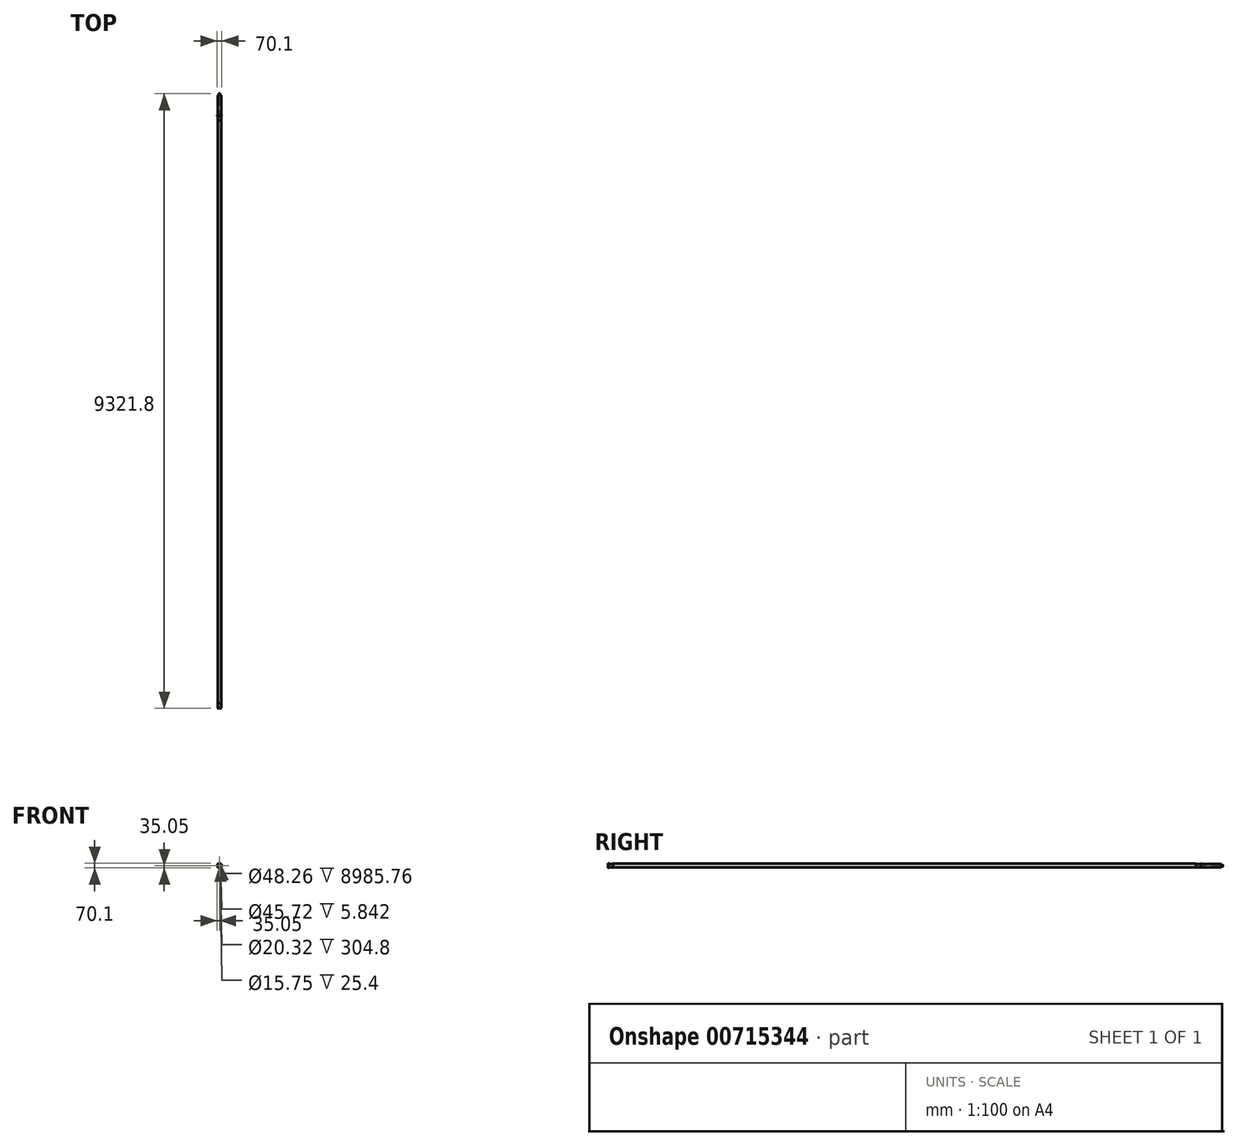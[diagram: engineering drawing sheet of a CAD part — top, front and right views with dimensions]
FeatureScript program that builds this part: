
annotation { "Feature Type Name" : "Feature", "Feature Type Description" : "" }
export const myFeature = defineFeature(function(context is Context, id is Id, definition is map)
    precondition{}
    {
        {
            var Q0;
            Q0=qCreatedBy(makeId("Front.planeOp"),FACE);
            var sketch = newSketch(context, id + "F0", { "sketchPlane" : qUnion([Q0])});
            skCircle(sketch, "E0", {"center": v(0, 0) * mm, "radius": 22.23 * mm, "construction": true});
            skSolve(sketch);
        }
        {
            var Q0;
            Q0=qCreatedBy(makeId("Front.planeOp"),FACE);
            var sketch = newSketch(context, id + "F1", { "sketchPlane" : qUnion([Q0])});
            skCircle(sketch, "E1", {"center": v(0, 0) * mm, "radius": 24.13 * mm});
            skCircle(sketch, "E2", {"center": v(0, 0) * mm, "radius": 35.05 * mm});
            skSolve(sketch);
        }
        {
            var Q0;
            Q0=qSketchRegion(id+"F1",true);
            extrude(context, id + "F2", {"entities" : qUnion([Q0]), "oppositeDirection" : true, "depth" : 5.84 * mm, "offsetDistance" : 25.4 * mm});
        }
        {
            var Q0;
            Q0=makeQuery(id+"F2.opExtrude","CAP_EDGE",EDGE,{"disambiguationData":[OSD([sQuery(id+"F1.wireOp",EDGE,"E2")])],"isStart":false});
            chamfer(context, id + "F3", {"entities" : qUnion([Q0]), "chamferType" : ChamferType.OFFSET_ANGLE, "width" : 2.54 * mm, "oppositeDirection" : false, "angle" : 70 * degree, "tangentPropagation" : true});
        }
        {
            var Q0;
            Q0=makeQuery(id+"F2.opExtrude","CAP_FACE",FACE,{"disambiguationData":[OSD([sQuery(id+"F1.wireOp",EDGE,"E1"),sQuery(id+"F1.wireOp",EDGE,"E2")])],"isStart":false});
            var sketch = newSketch(context, id + "F4", { "sketchPlane" : qUnion([Q0])});
            skCircle(sketch, "E3", {"center": v(0, 0) * mm, "radius": 28.07 * mm});
            skCircle(sketch, "E4", {"center": v(0, 0) * mm, "radius": 24.13 * mm});
            skSolve(sketch);
        }
        {
            var Q0;
            Q0=qSketchRegion(id+"F4",true);
            extrude(context, id + "F5", {"entities" : qUnion([Q0]), "operationType" : NewBodyOperationType.ADD, "depth" : 2.54 * mm, "offsetDistance" : 25.4 * mm});
        }
        {
            var Q0;
            Q0=makeQuery(id+"F5.opExtrude","CAP_FACE",FACE,{"disambiguationData":[OSD([sQuery(id+"F4.wireOp",EDGE,"E3"),sQuery(id+"F4.wireOp",EDGE,"E4")])],"isStart":false});
            var sketch = newSketch(context, id + "F6", { "sketchPlane" : qUnion([Q0])});
            skCircle(sketch, "E5", {"center": v(0, 0) * mm, "radius": 26.55 * mm});
            skCircle(sketch, "E6", {"center": v(0, 0) * mm, "radius": 24.13 * mm});
            skSolve(sketch);
        }
        {
            var Q0;
            Q0=qSketchRegion(id+"F6",true);
            extrude(context, id + "F7", {"entities" : qUnion([Q0]), "operationType" : NewBodyOperationType.ADD, "depth" : 2.54 * mm, "offsetDistance" : 25.4 * mm});
        }
        {
            var Q0;
            Q0=makeQuery(id+"F7.opExtrude","CAP_FACE",FACE,{"disambiguationData":[OSD([sQuery(id+"F6.wireOp",EDGE,"E5"),sQuery(id+"F6.wireOp",EDGE,"E6")])],"isStart":false});
            var sketch = newSketch(context, id + "F8", { "sketchPlane" : qUnion([Q0])});
            skCircle(sketch, "E7", {"center": v(0, 0) * mm, "radius": 24.13 * mm});
            skCircle(sketch, "E8", {"center": v(0, 0) * mm, "radius": 25.4 * mm});
            skSolve(sketch);
        }
        {
            var Q0;
            Q0=qSketchRegion(id+"F8",true);
            extrude(context, id + "F9", {"entities" : qUnion([Q0]), "operationType" : NewBodyOperationType.ADD, "depth" : 65.28 * mm, "offsetDistance" : 25.4 * mm});
        }
        {
            var Q0;
            Q0=makeQuery(id+"F9.opExtrude","CAP_FACE",FACE,{"disambiguationData":[OSD([sQuery(id+"F8.wireOp",EDGE,"E7"),sQuery(id+"F8.wireOp",EDGE,"E8")])],"isStart":false});
            var sketch = newSketch(context, id + "F10", { "sketchPlane" : qUnion([Q0])});
            skCircle(sketch, "E9", {"center": v(0, 0) * mm, "radius": 27.94 * mm});
            skCircle(sketch, "E10", {"center": v(0, 0) * mm, "radius": 24.13 * mm});
            skSolve(sketch);
        }
        {
            var Q0;
            Q0=qCreatedBy(makeId("Right.planeOp"),FACE);
            var sketch = newSketch(context, id + "F11", { "sketchPlane" : qUnion([Q0])});
            skLineSegment(sketch, "E11", {"start": v(76.2, 0) * mm, "end": v(8915.4, 0) * mm});
            skSolve(sketch);
        }
        {
            var Q0;
            Q0=qSketchRegion(id+"F10",true);
            var Q1;
            Q1=qConstructionFilter(qBodyType(qCreatedBy(id+"F11",EDGE),BodyType.WIRE),ConstructionObject.NO);
            sweep(context, id + "F12", {"operationType" : NewBodyOperationType.ADD, "profiles" : qUnion([Q0]), "path" : qUnion([Q1])});
        }
        {
            var Q0;
            Q0=makeQuery(id+"F12.opSweep","CAP_FACE",FACE,{"disambiguationData":[OSD([sQuery(id+"F10.wireOp",EDGE,"E9"),sQuery(id+"F10.wireOp",EDGE,"E10"),sQuery(id+"F11.wireOp",VERTEX,"7ykRA0Qg-2DrY-rTCa-7tXY-ZQoEE0Xzwcjr.end")])],"isStart":false});
            var sketch = newSketch(context, id + "F13", { "sketchPlane" : qUnion([Q0])});
            skCircle(sketch, "E12", {"center": v(0, 0) * mm, "radius": 24.13 * mm});
            skCircle(sketch, "E13", {"center": v(0, 0) * mm, "radius": 25.4 * mm});
            skSolve(sketch);
        }
        {
            var Q0;
            Q0=makeQuery(id+"F12.opSweep","CAP_EDGE",EDGE,{"disambiguationData":[OSD([sQuery(id+"F10.wireOp",EDGE,"E9"),sQuery(id+"F11.wireOp",VERTEX,"7ykRA0Qg-2DrY-rTCa-7tXY-ZQoEE0Xzwcjr.end")])],"isStart":false});
            fillet(context, id + "F14", {"entities" : qUnion([Q0]), "radius" : 1.27 * mm, "tangentPropagation" : true, "allowEdgeOverflow" : false});
        }
        {
            var Q0;
            Q0=qSketchRegion(id+"F13",true);
            extrude(context, id + "F15", {"entities" : qUnion([Q0]), "operationType" : NewBodyOperationType.ADD, "depth" : 76.2 * mm, "offsetDistance" : 25.4 * mm});
        }
        {
            var Q0;
            Q0=makeQuery(id+"F15.opExtrude","CAP_FACE",FACE,{"disambiguationData":[OSD([sQuery(id+"F13.wireOp",EDGE,"E12"),sQuery(id+"F13.wireOp",EDGE,"E13")])],"isStart":false});
            var sketch = newSketch(context, id + "F16", { "sketchPlane" : qUnion([Q0])});
            skCircle(sketch, "E14", {"center": v(0, 0) * mm, "radius": 35.05 * mm});
            skCircle(sketch, "E15", {"center": v(0, 0) * mm, "radius": 22.86 * mm});
            skSolve(sketch);
        }
        {
            var Q0;
            Q0=qSketchRegion(id+"F16",true);
            extrude(context, id + "F17", {"entities" : qUnion([Q0]), "operationType" : NewBodyOperationType.ADD, "oppositeDirection" : true, "depth" : 5.84 * mm, "offsetDistance" : 25.4 * mm});
        }
        {
            var Q0;
            Q0=makeQuery(id+"F17.opExtrude","CAP_EDGE",EDGE,{"disambiguationData":[OSD([sQuery(id+"F16.wireOp",EDGE,"E14")])],"isStart":false});
            chamfer(context, id + "F18", {"entities" : qUnion([Q0]), "chamferType" : ChamferType.OFFSET_ANGLE, "width" : 2.54 * mm, "oppositeDirection" : false, "angle" : 70 * degree, "tangentPropagation" : true});
        }
        {
            var Q0;
            Q0=makeQuery(id+"F17.opExtrude","CAP_FACE",FACE,{"disambiguationData":[OSD([sQuery(id+"F16.wireOp",EDGE,"E14"),sQuery(id+"F16.wireOp",EDGE,"E15")])],"isStart":false});
            var sketch = newSketch(context, id + "F19", { "sketchPlane" : qUnion([Q0])});
            skCircle(sketch, "E16", {"center": v(0, 0) * mm, "radius": 24.13 * mm});
            skCircle(sketch, "E17", {"center": v(0, 0) * mm, "radius": 28.07 * mm});
            skSolve(sketch);
        }
        {
            var Q0;
            Q0=qSketchRegion(id+"F19",true);
            extrude(context, id + "F20", {"entities" : qUnion([Q0]), "operationType" : NewBodyOperationType.ADD, "depth" : 2.54 * mm, "offsetDistance" : 25.4 * mm});
        }
        {
            var Q0;
            Q0=makeQuery(id+"F20.opExtrude","CAP_FACE",FACE,{"disambiguationData":[OSD([sQuery(id+"F19.wireOp",EDGE,"E16"),sQuery(id+"F19.wireOp",EDGE,"E17")])],"isStart":false});
            var sketch = newSketch(context, id + "F21", { "sketchPlane" : qUnion([Q0])});
            skCircle(sketch, "E18", {"center": v(0, 0) * mm, "radius": 24.13 * mm});
            skCircle(sketch, "E19", {"center": v(0, 0) * mm, "radius": 26.8 * mm});
            skSolve(sketch);
        }
        {
            var Q0;
            Q0=qSketchRegion(id+"F21",true);
            extrude(context, id + "F22", {"entities" : qUnion([Q0]), "operationType" : NewBodyOperationType.ADD, "depth" : 2.54 * mm, "offsetDistance" : 25.4 * mm});
        }
        {
            var Q0;
            Q0=makeQuery(id+"F17.boolean.opBoolean","MERGE",FACE,{"derivedFrom":[makeQuery(id+"F15.opExtrude","CAP_FACE",FACE,{"disambiguationData":[OSD([sQuery(id+"F13.wireOp",EDGE,"E12"),sQuery(id+"F13.wireOp",EDGE,"E13")])],"isStart":false}),makeQuery(id+"F17.opExtrude","CAP_FACE",FACE,{"disambiguationData":[OSD([sQuery(id+"F16.wireOp",EDGE,"E14"),sQuery(id+"F16.wireOp",EDGE,"E15")])],"isStart":true})]});
            var sketch = newSketch(context, id + "F23", { "sketchPlane" : qUnion([Q0])});
            skCircle(sketch, "E20", {"center": v(0, 0) * mm, "radius": 10.16 * mm});
            skCircle(sketch, "E21", {"center": v(0, 0) * mm, "radius": 24.13 * mm});
            skSolve(sketch);
        }
        {
            var Q0;
            Q0=qSketchRegion(id+"F23",true);
            extrude(context, id + "F24", {"entities" : qUnion([Q0]), "operationType" : NewBodyOperationType.ADD, "depth" : 304.8 * mm, "offsetDistance" : 25.4 * mm});
        }
        {
            var Q0;
            Q0=makeQuery(id+"F24.opExtrude","CAP_FACE",FACE,{"disambiguationData":[OSD([sQuery(id+"F23.wireOp",EDGE,"E20"),sQuery(id+"F23.wireOp",EDGE,"E21")])],"isStart":false});
            var sketch = newSketch(context, id + "F25", { "sketchPlane" : qUnion([Q0])});
            skCircle(sketch, "E22", {"center": v(0, 0) * mm, "radius": 10.67 * mm});
            skCircle(sketch, "E23", {"center": v(0, 0) * mm, "radius": 7.87 * mm});
            skSolve(sketch);
        }
        {
            var Q0;
            Q0=qSketchRegion(id+"F25",true);
            extrude(context, id + "F26", {"entities" : qUnion([Q0]), "operationType" : NewBodyOperationType.ADD, "depth" : 25.4 * mm, "offsetDistance" : 25.4 * mm});
        }
    });
